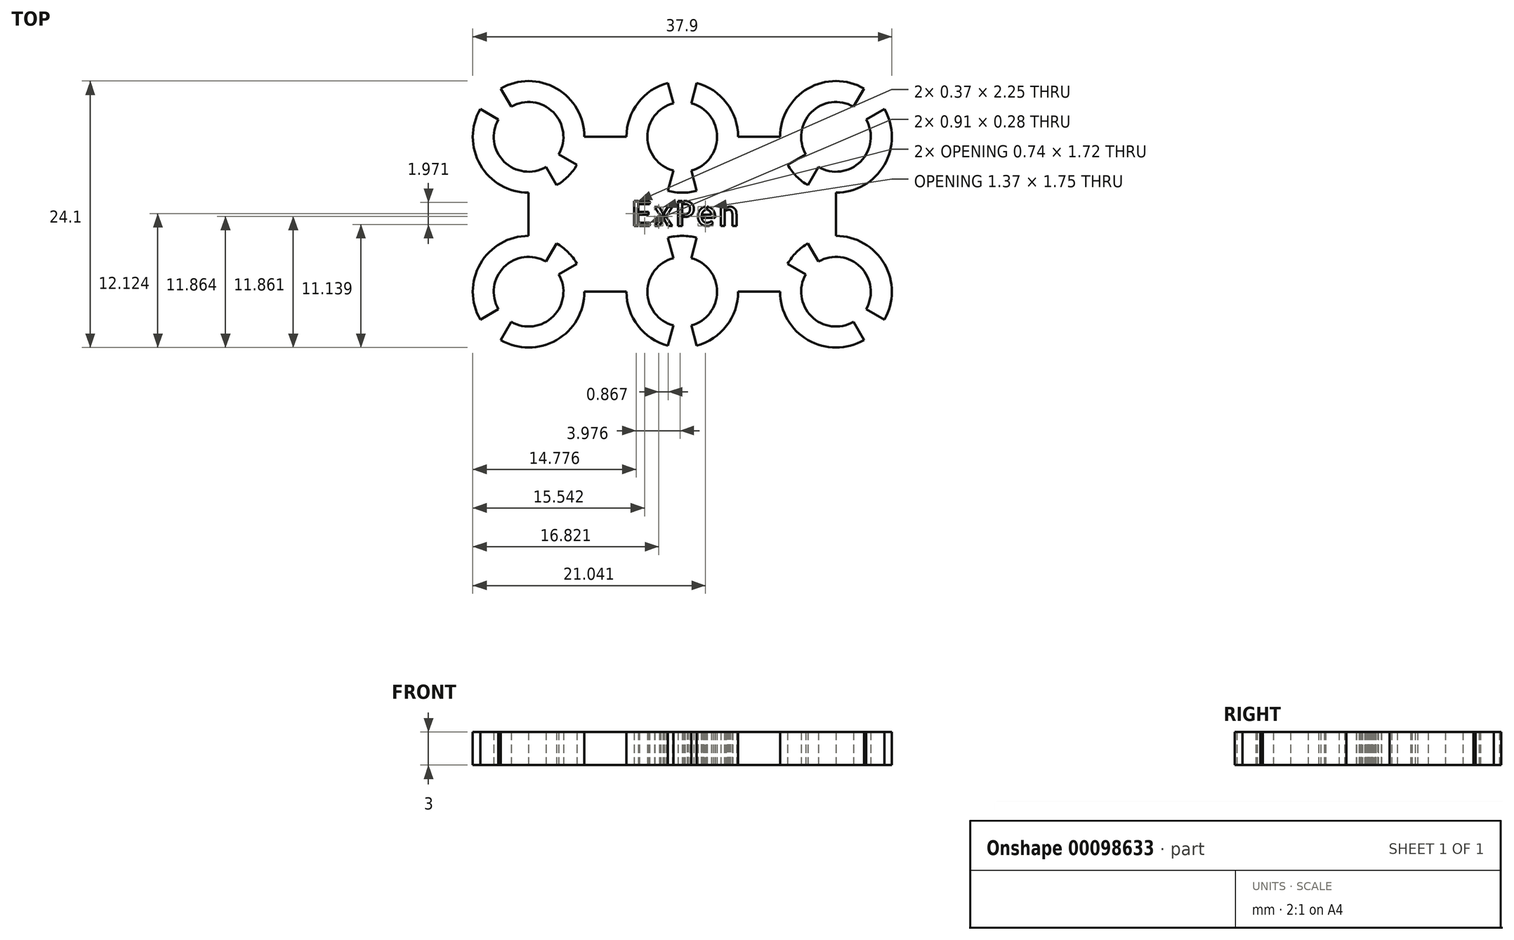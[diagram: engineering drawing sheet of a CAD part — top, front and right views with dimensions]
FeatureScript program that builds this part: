
annotation { "Feature Type Name" : "Feature", "Feature Type Description" : "" }
export const myFeature = defineFeature(function(context is Context, id is Id, definition is map)
    precondition{}
    {
        {
            var Q0;
            Q0=qCreatedBy(makeId("Top.planeOp"),FACE);
            var sketch = newSketch(context, id + "F0", { "sketchPlane" : qUnion([Q0])});
            skCircle(sketch, "E0", {"center": v(0, 0) * mm, "radius": 3.15 * mm});
            skCircle(sketch, "E1", {"center": v(13.9, 0) * mm, "radius": 3.15 * mm});
            skCircle(sketch, "E2", {"center": v(-13.9, 0) * mm, "radius": 3.15 * mm});
            skCircle(sketch, "E3", {"center": v(0, 14) * mm, "radius": 3.15 * mm});
            skCircle(sketch, "E4", {"center": v(-13.9, 14) * mm, "radius": 3.15 * mm});
            skCircle(sketch, "E5", {"center": v(13.9, 14) * mm, "radius": 3.15 * mm});
            skCircle(sketch, "E6.0", {"center": v(-13.9, 14) * mm, "radius": 5.05 * mm});
            skCircle(sketch, "E7.0", {"center": v(0, 14) * mm, "radius": 5.05 * mm});
            skCircle(sketch, "E8.0", {"center": v(13.9, 14) * mm, "radius": 5.05 * mm});
            skCircle(sketch, "E9.0", {"center": v(-13.9, 0) * mm, "radius": 5.05 * mm});
            skCircle(sketch, "E10.0", {"center": v(0, 0) * mm, "radius": 5.05 * mm});
            skCircle(sketch, "E11.0", {"center": v(13.9, 0) * mm, "radius": 5.05 * mm});
            skLineSegment(sketch, "E12", {"start": v(-13.9, 8.95) * mm, "end": v(-13.9, 5.05) * mm});
            skLineSegment(sketch, "E13", {"start": v(13.9, 8.95) * mm, "end": v(13.9, 5.05) * mm});
            skLineSegment(sketch, "E14", {"start": v(-8.85, 14) * mm, "end": v(-5.05, 14) * mm});
            skLineSegment(sketch, "E15", {"start": v(5.05, 14) * mm, "end": v(8.85, 14) * mm});
            skLineSegment(sketch, "E16", {"start": v(-8.85, 0) * mm, "end": v(-5.05, 0) * mm});
            skLineSegment(sketch, "E17", {"start": v(5.05, 0) * mm, "end": v(8.85, 0) * mm});
            skText(sketch, "E18", { "text": "ExPen", "fontName": "AllertaStencil-Regular.ttf"});
            skLineSegment(sketch, "E19", {"start": v(0, -5.05) * mm, "end": v(0, 5.05) * mm, "construction": true});
            skLineSegment(sketch, "E20", {"start": v(0, 0) * mm, "end": v(-1.3, -4.88) * mm});
            skLineSegment(sketch, "E21", {"start": v(0, 0) * mm, "end": v(1.3, -4.88) * mm});
            skLineSegment(sketch, "E22", {"start": v(0, 0) * mm, "end": v(1.3, 4.88) * mm});
            skLineSegment(sketch, "E23", {"start": v(0, 0) * mm, "end": v(-1.3, 4.88) * mm});
            skLineSegment(sketch, "E24", {"start": v(0, 14) * mm, "end": v(0, 19.05) * mm});
            skLineSegment(sketch, "E25", {"start": v(0, 19.05) * mm, "end": v(0, 8.95) * mm, "construction": true});
            skLineSegment(sketch, "E26", {"start": v(0, 14) * mm, "end": v(-1.3, 9.12) * mm});
            skLineSegment(sketch, "E27", {"start": v(0, 14) * mm, "end": v(1.3, 9.12) * mm});
            skLineSegment(sketch, "E28", {"start": v(0, 14) * mm, "end": v(-1.3, 18.88) * mm});
            skLineSegment(sketch, "E29", {"start": v(0, 14) * mm, "end": v(1.3, 18.88) * mm});
            skLineSegment(sketch, "E30", {"start": v(-13.9, 0) * mm, "end": v(-10.33, 3.57) * mm, "construction": true});
            skLineSegment(sketch, "E31", {"start": v(-13.9, 0) * mm, "end": v(-17.47, -3.57) * mm, "construction": true});
            skLineSegment(sketch, "E32", {"start": v(-13.9, 0) * mm, "end": v(-9.53, 2.53) * mm});
            skLineSegment(sketch, "E33", {"start": v(-13.9, 0) * mm, "end": v(-11.38, 4.37) * mm});
            skLineSegment(sketch, "E34", {"start": v(-13.9, 0) * mm, "end": v(-16.42, -4.37) * mm});
            skLineSegment(sketch, "E35", {"start": v(-13.9, 0) * mm, "end": v(-18.27, -2.53) * mm});
            skLineSegment(sketch, "E36", {"start": v(-17.47, 17.57) * mm, "end": v(-13.9, 14) * mm, "construction": true});
            skLineSegment(sketch, "E37", {"start": v(-17.47, 17.57) * mm, "end": v(-10.33, 10.43) * mm, "construction": true});
            skLineSegment(sketch, "E38", {"start": v(-18.27, 16.52) * mm, "end": v(-13.9, 14) * mm});
            skLineSegment(sketch, "E39", {"start": v(-13.9, 14) * mm, "end": v(-9.53, 11.47) * mm});
            skLineSegment(sketch, "E40", {"start": v(-16.42, 18.37) * mm, "end": v(-13.9, 14) * mm});
            skLineSegment(sketch, "E41", {"start": v(-13.9, 14) * mm, "end": v(-11.37, 9.63) * mm});
            skLineSegment(sketch, "E42", {"start": v(10.33, 10.43) * mm, "end": v(13.9, 14) * mm, "construction": true});
            skLineSegment(sketch, "E43", {"start": v(13.9, 14) * mm, "end": v(17.47, 17.57) * mm, "construction": true});
            skLineSegment(sketch, "E44", {"start": v(16.42, 18.37) * mm, "end": v(13.9, 14) * mm});
            skLineSegment(sketch, "E45", {"start": v(13.9, 14) * mm, "end": v(11.38, 9.63) * mm});
            skLineSegment(sketch, "E46", {"start": v(13.9, 14) * mm, "end": v(9.53, 11.47) * mm});
            skLineSegment(sketch, "E47", {"start": v(13.9, 14) * mm, "end": v(18.27, 16.53) * mm});
            skLineSegment(sketch, "E48", {"start": v(13.9, 0) * mm, "end": v(10.33, 3.57) * mm, "construction": true});
            skLineSegment(sketch, "E49", {"start": v(13.9, 0) * mm, "end": v(17.47, -3.57) * mm, "construction": true});
            skLineSegment(sketch, "E50", {"start": v(13.9, 0) * mm, "end": v(9.53, 2.52) * mm});
            skLineSegment(sketch, "E51", {"start": v(13.9, 0) * mm, "end": v(18.27, -2.52) * mm});
            skLineSegment(sketch, "E52", {"start": v(13.9, 0) * mm, "end": v(16.43, -4.37) * mm});
            skLineSegment(sketch, "E53", {"start": v(13.9, 0) * mm, "end": v(11.37, 4.37) * mm});
            const initialGuessF0  = {"E18": [-0.00465, 0.00595, 1, 0, 0.00225]};
            skSetInitialGuess(sketch, initialGuessF0);
            skSolve(sketch);
        }
        {
            var Q0;
            {var subQ10=sQuery(id+"F0.wireOp",EDGE,"E12");Q0=makeQuery(id+"F0.imprint","IMPRINT",FACE,{"disambiguationData":[TD([[makeQuery(id+"F0.imprint","IMPRINT",EDGE,{"derivedFrom":subQ10}),1.0]])]});}
            var Q1;
            {var subQ10=sQuery(id+"F0.wireOp",EDGE,"E12");Q1=makeQuery(id+"F0.imprint","IMPRINT",FACE,{"disambiguationData":[TD([[makeQuery(id+"F0.imprint","IMPRINT",EDGE,{"derivedFrom":subQ10}),1.0]])]});}
            var Q2;
            {var subQ3=sQuery(id+"F0.wireOp",EDGE,"E0");var subQ6=sQuery(id+"F0.wireOp",EDGE,"E22");var subQ8=makeQuery(id+"F0.imprint","INTERSECT",VERTEX,{"derivedFrom":[subQ3,subQ6]});Q2=makeQuery(id+"F0.imprint","IMPRINT",FACE,{"disambiguationData":[TD([[makeQuery(id+"F0.imprint","IMPRINT",EDGE,{"disambiguationData":[TD([[subQ8,1.0]])],"derivedFrom":subQ3}),-1.0]])]});}
            var Q3;
            {var subQ3=sQuery(id+"F0.wireOp",EDGE,"E0");var subQ6=sQuery(id+"F0.wireOp",EDGE,"E23");var subQ8=makeQuery(id+"F0.imprint","INTERSECT",VERTEX,{"derivedFrom":[subQ3,subQ6]});Q3=makeQuery(id+"F0.imprint","IMPRINT",FACE,{"disambiguationData":[TD([[makeQuery(id+"F0.imprint","IMPRINT",EDGE,{"disambiguationData":[TD([[subQ8,-1.0]])],"derivedFrom":subQ3}),-1.0]])]});}
            var Q4;
            {var subQ4=sQuery(id+"F0.wireOp",EDGE,"E28");var subQ6=sQuery(id+"F0.wireOp",EDGE,"E3");var subQ8=makeQuery(id+"F0.imprint","INTERSECT",VERTEX,{"derivedFrom":[subQ6,subQ4]});Q4=makeQuery(id+"F0.imprint","IMPRINT",FACE,{"disambiguationData":[TD([[makeQuery(id+"F0.imprint","IMPRINT",EDGE,{"disambiguationData":[TD([[subQ8,-1.0]])],"derivedFrom":subQ6}),-1.0]])]});}
            var Q5;
            {var subQ3=sQuery(id+"F0.wireOp",EDGE,"E3");var subQ6=sQuery(id+"F0.wireOp",EDGE,"E29");var subQ8=makeQuery(id+"F0.imprint","INTERSECT",VERTEX,{"derivedFrom":[subQ3,subQ6]});Q5=makeQuery(id+"F0.imprint","IMPRINT",FACE,{"disambiguationData":[TD([[makeQuery(id+"F0.imprint","IMPRINT",EDGE,{"disambiguationData":[TD([[subQ8,1.0]])],"derivedFrom":subQ3}),-1.0]])]});}
            var Q6;
            {var subQ0=sQuery(id+"F0.wireOp",EDGE,"E33");var subQ3=sQuery(id+"F0.wireOp",EDGE,"E2");var subQ4=makeQuery(id+"F0.imprint","INTERSECT",VERTEX,{"derivedFrom":[subQ3,subQ0]});Q6=makeQuery(id+"F0.imprint","IMPRINT",FACE,{"disambiguationData":[TD([[makeQuery(id+"F0.imprint","IMPRINT",EDGE,{"disambiguationData":[TD([[subQ4,-1.0]])],"derivedFrom":subQ3}),-1.0]])]});}
            var Q7;
            {var subQ0=sQuery(id+"F0.wireOp",EDGE,"E32");var subQ3=sQuery(id+"F0.wireOp",EDGE,"E2");var subQ4=makeQuery(id+"F0.imprint","INTERSECT",VERTEX,{"derivedFrom":[subQ3,subQ0]});Q7=makeQuery(id+"F0.imprint","IMPRINT",FACE,{"disambiguationData":[TD([[makeQuery(id+"F0.imprint","IMPRINT",EDGE,{"disambiguationData":[TD([[subQ4,1.0]])],"derivedFrom":subQ3}),-1.0]])]});}
            var Q8;
            {var subQ0=sQuery(id+"F0.wireOp",EDGE,"E38");var subQ3=sQuery(id+"F0.wireOp",EDGE,"E4");var subQ4=makeQuery(id+"F0.imprint","INTERSECT",VERTEX,{"derivedFrom":[subQ3,subQ0]});Q8=makeQuery(id+"F0.imprint","IMPRINT",FACE,{"disambiguationData":[TD([[makeQuery(id+"F0.imprint","IMPRINT",EDGE,{"disambiguationData":[TD([[subQ4,-1.0]])],"derivedFrom":subQ3}),-1.0]])]});}
            var Q9;
            {var subQ3=sQuery(id+"F0.wireOp",EDGE,"E4");var subQ5=sQuery(id+"F0.wireOp",EDGE,"E40");var subQ6=makeQuery(id+"F0.imprint","INTERSECT",VERTEX,{"derivedFrom":[subQ3,subQ5]});Q9=makeQuery(id+"F0.imprint","IMPRINT",FACE,{"disambiguationData":[TD([[makeQuery(id+"F0.imprint","IMPRINT",EDGE,{"disambiguationData":[TD([[subQ6,1.0]])],"derivedFrom":subQ3}),-1.0]])]});}
            var Q10;
            {var subQ0=sQuery(id+"F0.wireOp",EDGE,"E44");var subQ3=sQuery(id+"F0.wireOp",EDGE,"E5");var subQ4=makeQuery(id+"F0.imprint","INTERSECT",VERTEX,{"derivedFrom":[subQ3,subQ0]});Q10=makeQuery(id+"F0.imprint","IMPRINT",FACE,{"disambiguationData":[TD([[makeQuery(id+"F0.imprint","IMPRINT",EDGE,{"disambiguationData":[TD([[subQ4,-1.0]])],"derivedFrom":subQ3}),-1.0]])]});}
            var Q11;
            {var subQ3=sQuery(id+"F0.wireOp",EDGE,"E5");var subQ6=sQuery(id+"F0.wireOp",EDGE,"E47");var subQ8=makeQuery(id+"F0.imprint","INTERSECT",VERTEX,{"derivedFrom":[subQ3,subQ6]});Q11=makeQuery(id+"F0.imprint","IMPRINT",FACE,{"disambiguationData":[TD([[makeQuery(id+"F0.imprint","IMPRINT",EDGE,{"disambiguationData":[TD([[subQ8,1.0]])],"derivedFrom":subQ3}),-1.0]])]});}
            var Q12;
            {var subQ3=sQuery(id+"F0.wireOp",EDGE,"E1");var subQ6=sQuery(id+"F0.wireOp",EDGE,"E53");var subQ8=makeQuery(id+"F0.imprint","INTERSECT",VERTEX,{"derivedFrom":[subQ3,subQ6]});Q12=makeQuery(id+"F0.imprint","IMPRINT",FACE,{"disambiguationData":[TD([[makeQuery(id+"F0.imprint","IMPRINT",EDGE,{"disambiguationData":[TD([[subQ8,1.0]])],"derivedFrom":subQ3}),-1.0]])]});}
            var Q13;
            {var subQ0=sQuery(id+"F0.wireOp",EDGE,"E50");var subQ3=sQuery(id+"F0.wireOp",EDGE,"E1");var subQ4=makeQuery(id+"F0.imprint","INTERSECT",VERTEX,{"derivedFrom":[subQ3,subQ0]});Q13=makeQuery(id+"F0.imprint","IMPRINT",FACE,{"disambiguationData":[TD([[makeQuery(id+"F0.imprint","IMPRINT",EDGE,{"disambiguationData":[TD([[subQ4,-1.0]])],"derivedFrom":subQ3}),-1.0]])]});}
            extrude(context, id + "F1", {"entities" : qUnion([Q0, Q1, Q2, Q3, Q4, Q5, Q6, Q7, Q8, Q9, Q10, Q11, Q12, Q13]), "depth" : 3 * mm});
        }
    });
